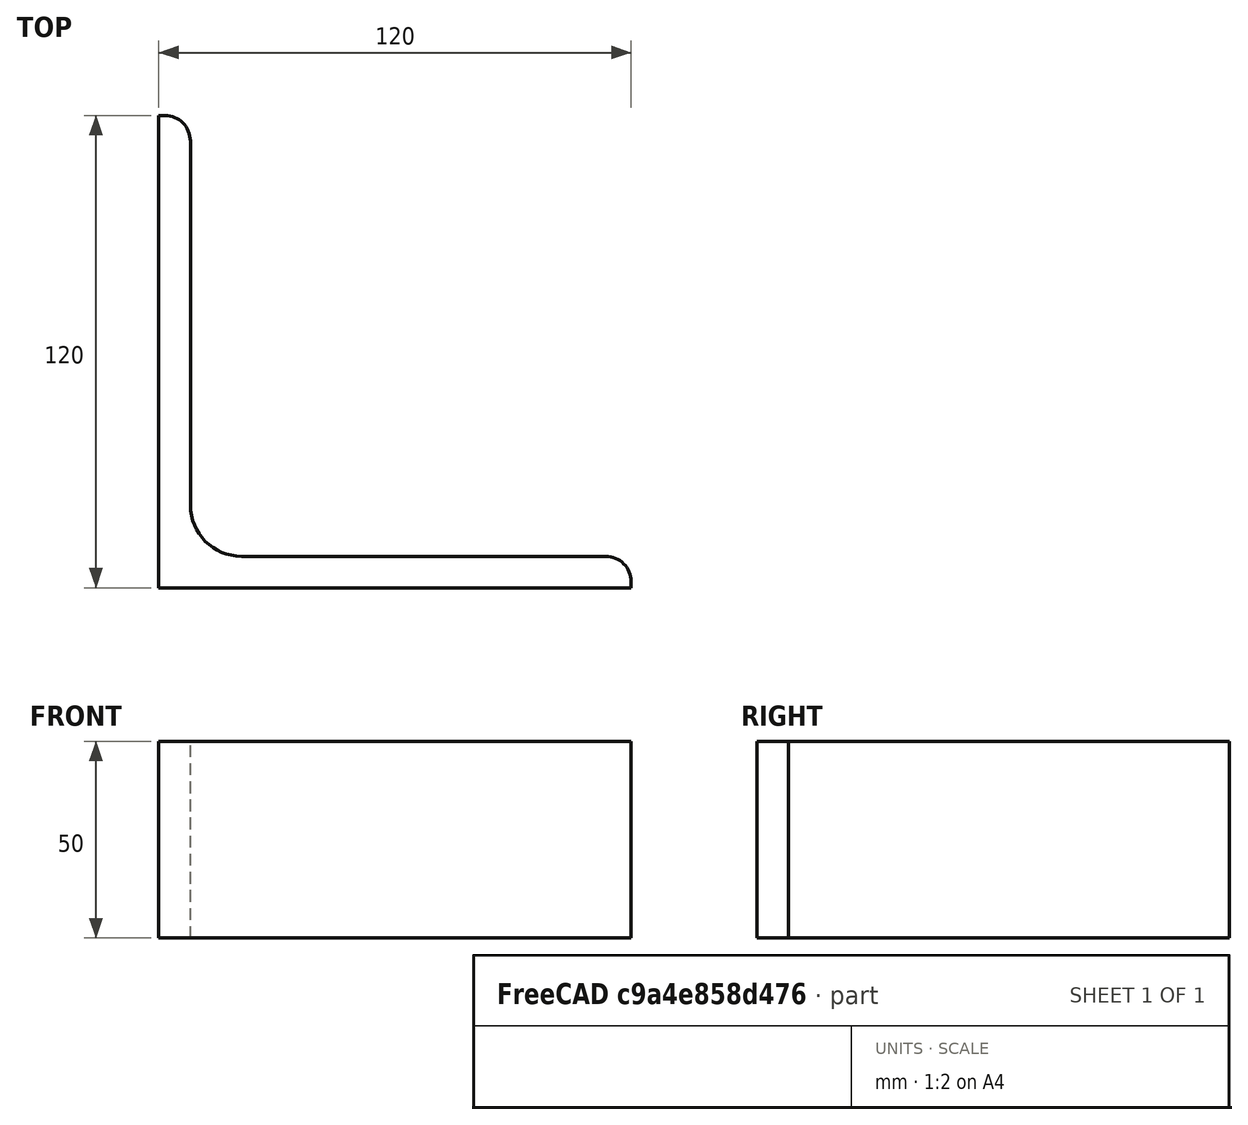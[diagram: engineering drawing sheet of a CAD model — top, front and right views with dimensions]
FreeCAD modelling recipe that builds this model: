
FCSTD DOCUMENT  (FreeCAD 0.15R4671 (Git))
Label: Angle Bar L120x120x8 EN10056 S235JR
License: All rights reserved
LicenseURL: http://en.wikipedia.org/wiki/All_rights_reserved
objects: Sketcher::SketchObject×1, Part::Extrusion×1
note: 2 computed .brp shape members not serialized (recipe doc carries the construction recipe); baked Part::Feature solids carry a one-line shape summary decoded from their .brp

FEATURE [Sketcher::SketchObject] Sketch
  sketch-geometry (9):
    g0: LineSegment StartX=0 StartY=0 StartZ=0 EndX=120 EndY=0 EndZ=0
    g1: LineSegment StartX=120 StartY=0 StartZ=0 EndX=120 EndY=1.5 EndZ=0
    g2: LineSegment StartX=113.5 StartY=8 StartZ=0 EndX=21 EndY=8 EndZ=0
    g3: LineSegment StartX=0 StartY=0 StartZ=0 EndX=0 EndY=120 EndZ=0
    g4: LineSegment StartX=0 StartY=120 StartZ=0 EndX=1.5 EndY=120 EndZ=0
    g5: LineSegment StartX=8 StartY=113.5 StartZ=0 EndX=8 EndY=21 EndZ=0
    g6: ArcOfCircle CenterX=21 CenterY=21 CenterZ=0 NormalX=0 NormalY=0 NormalZ=1 Radius=13 StartAngle=3.14159 EndAngle=4.71239
    g7: ArcOfCircle CenterX=1.5 CenterY=113.5 CenterZ=0 NormalX=0 NormalY=0 NormalZ=1 Radius=6.5 StartAngle=0 EndAngle=1.5708
    g8: ArcOfCircle CenterX=113.5 CenterY=1.5 CenterZ=0 NormalX=0 NormalY=0 NormalZ=1 Radius=6.5 StartAngle=0 EndAngle=1.5708
  constraints (23):
    c: Coincident(g0,g-1)
    c: Horizontal(g0)
    c: Coincident(g1,g0)
    c: Vertical(g1)
    c: Horizontal(g2)
    c: Coincident(g3,g-1)
    c: Vertical(g3)
    c: Coincident(g4,g3)
    c: Horizontal(g4)
    c: Vertical(g5)
    c: Tangent(g5,g6) = -1.5708
    c: Tangent(g2,g6) = 1.5708
    c: Tangent(g4,g7) = 1.5708
    c: Tangent(g5,g7) = 1.5708
    c: Tangent(g2,g8) = -1.5708
    c: Tangent(g1,g8) = -1.5708
    c: DistanceX(g0) = 120
    c: DistanceY(g3) = 120
    c: DistanceY(g0,g2) = 8
    c: DistanceX(g3,g5) = 8
    c: Radius(g6) = 13
    c: Radius(g8) = 6.5
    c: Radius(g7) = 6.5
FEATURE [Part::Extrusion] Extrude  label="Angle Bar L120x120x8 EN10056 S235JR"
  Base = -> Sketch
  Dir = (0,0,50)
  Solid = true
